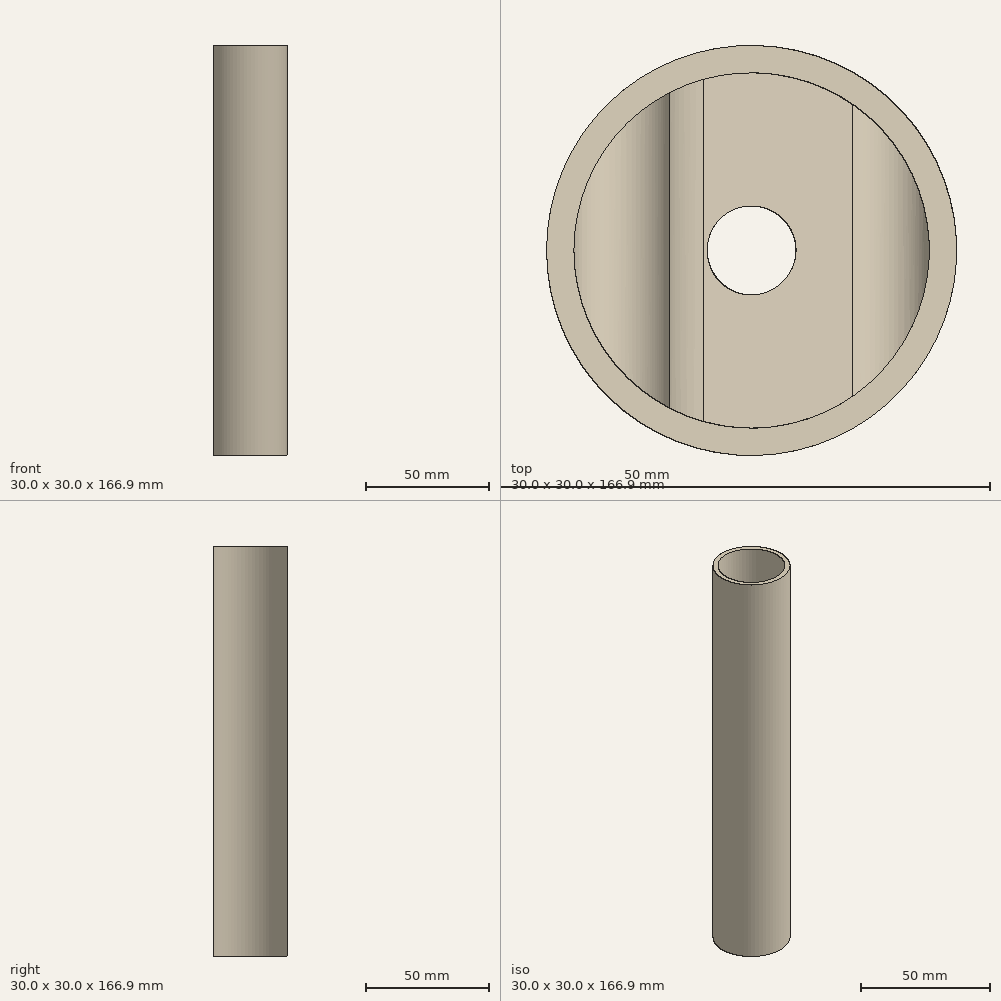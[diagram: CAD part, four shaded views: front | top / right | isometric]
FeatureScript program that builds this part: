
annotation { "Feature Type Name" : "Feature", "Feature Type Description" : "" }
export const myFeature = defineFeature(function(context is Context, id is Id, definition is map)
    precondition{}
    {
        {
            var Q0;
            Q0=qCreatedBy(makeId("Front.planeOp"),FACE);
            var sketch = newSketch(context, id + "F0", { "sketchPlane" : qUnion([Q0])});
            skLineSegment(sketch, "E0.bottom", {"start": v(15, 0) * mm, "end": v(0, 0) * mm, "construction": true});
            skLineSegment(sketch, "E0.top", {"start": v(15, 160) * mm, "end": v(0, 160) * mm, "construction": true});
            skLineSegment(sketch, "E0.left", {"start": v(15, 0) * mm, "end": v(15, 160) * mm, "construction": true});
            skLineSegment(sketch, "E0.right", {"start": v(0, 0) * mm, "end": v(0, 160) * mm, "construction": true});
            skLineSegment(sketch, "E1.MirrorCS", {"start": v(-15, 0) * mm, "end": v(-15, 160) * mm, "construction": true});
            skLineSegment(sketch, "E2", {"start": v(13, 0) * mm, "end": v(13, 160) * mm, "construction": true});
            skLineSegment(sketch, "E3.MirrorCS", {"start": v(-13, 0) * mm, "end": v(-13, 160) * mm, "construction": true});
            skLineSegment(sketch, "E4.MirrorCS", {"start": v(-15, 0) * mm, "end": v(0, 0) * mm, "construction": true});
            skLineSegment(sketch, "E5.MirrorCS", {"start": v(-15, 160) * mm, "end": v(0, 160) * mm, "construction": true});
            skLineSegment(sketch, "E6", {"start": v(3.5, 0) * mm, "end": v(3.5, 160) * mm, "construction": true});
            skLineSegment(sketch, "E7.MirrorCS", {"start": v(-3.5, 0) * mm, "end": v(-3.5, 160) * mm, "construction": true});
            skSolve(sketch);
        }
        {
            var Q0;
            Q0=qCreatedBy(makeId("Front.planeOp"),FACE);
            var sketch = newSketch(context, id + "F1", { "sketchPlane" : qUnion([Q0])});
            skArc(sketch, "E8", {"start": v(-13.08, 33) * mm, "mid": v(-9.35, 29.44) * mm, "end": v(-6, 33.35) * mm});
            skArc(sketch, "E9", {"start": v(-13.08, 23.7) * mm, "mid": v(-10.14, 27.9) * mm, "end": v(-5.15, 26.66) * mm});
            skArc(sketch, "E10", {"start": v(7.37, 17.07) * mm, "mid": v(10.97, 16.65) * mm, "end": v(12.98, 19.67) * mm});
            skArc(sketch, "E11", {"start": v(12.98, 9.26) * mm, "mid": v(11.86, 12.31) * mm, "end": v(8.97, 13.81) * mm});
            skArc(sketch, "E12", {"start": v(8.97, 13.81) * mm, "mid": v(7.8, 14.12) * mm, "end": v(6.74, 14.74) * mm});
            skArc(sketch, "E13", {"start": v(-6, 33.35) * mm, "mid": v(-5.17, 30.52) * mm, "end": v(-3.56, 28.05) * mm});
            skLineSegment(sketch, "E14", {"start": v(-13.08, 33) * mm, "end": v(-13.08, 23.7) * mm});
            skLineSegment(sketch, "E15", {"start": v(-3.56, 28.05) * mm, "end": v(7.37, 17.07) * mm});
            skLineSegment(sketch, "E16", {"start": v(-5.15, 26.66) * mm, "end": v(6.74, 14.74) * mm});
            skLineSegment(sketch, "E17", {"start": v(12.98, 9.26) * mm, "end": v(12.98, 19.67) * mm});
            skArc(sketch, "E18", {"start": v(-13.08, 54.39) * mm, "mid": v(-9.35, 50.84) * mm, "end": v(-6, 54.74) * mm});
            skArc(sketch, "E19", {"start": v(-13.08, 45.09) * mm, "mid": v(-10.14, 49.3) * mm, "end": v(-5.15, 48.06) * mm});
            skArc(sketch, "E20", {"start": v(7.37, 38.46) * mm, "mid": v(10.97, 38.05) * mm, "end": v(12.98, 41.07) * mm});
            skArc(sketch, "E21", {"start": v(12.98, 30.65) * mm, "mid": v(11.86, 33.7) * mm, "end": v(8.97, 35.2) * mm});
            skArc(sketch, "E22", {"start": v(8.97, 35.2) * mm, "mid": v(7.8, 35.52) * mm, "end": v(6.74, 36.14) * mm});
            skArc(sketch, "E23", {"start": v(-6, 54.74) * mm, "mid": v(-5.17, 51.91) * mm, "end": v(-3.56, 49.44) * mm});
            skLineSegment(sketch, "E24", {"start": v(-13.08, 54.39) * mm, "end": v(-13.08, 45.09) * mm});
            skLineSegment(sketch, "E25", {"start": v(-3.56, 49.44) * mm, "end": v(7.37, 38.46) * mm});
            skLineSegment(sketch, "E26", {"start": v(-5.15, 48.06) * mm, "end": v(6.74, 36.14) * mm});
            skLineSegment(sketch, "E27", {"start": v(12.98, 30.65) * mm, "end": v(12.98, 41.07) * mm});
            skArc(sketch, "E28", {"start": v(-13.08, 78.1) * mm, "mid": v(-9.35, 74.56) * mm, "end": v(-6, 78.46) * mm});
            skArc(sketch, "E29", {"start": v(-13.08, 68.8) * mm, "mid": v(-10.14, 73.02) * mm, "end": v(-5.15, 71.78) * mm});
            skArc(sketch, "E30", {"start": v(7.37, 62.18) * mm, "mid": v(10.97, 61.77) * mm, "end": v(12.98, 64.79) * mm});
            skArc(sketch, "E31", {"start": v(12.98, 54.37) * mm, "mid": v(11.86, 57.42) * mm, "end": v(8.97, 58.93) * mm});
            skArc(sketch, "E32", {"start": v(8.97, 58.93) * mm, "mid": v(7.8, 59.24) * mm, "end": v(6.74, 59.86) * mm});
            skArc(sketch, "E33", {"start": v(-6, 78.46) * mm, "mid": v(-5.17, 75.63) * mm, "end": v(-3.56, 73.16) * mm});
            skLineSegment(sketch, "E34", {"start": v(-13.08, 78.1) * mm, "end": v(-13.08, 68.8) * mm});
            skLineSegment(sketch, "E35", {"start": v(-3.56, 73.16) * mm, "end": v(7.37, 62.18) * mm});
            skLineSegment(sketch, "E36", {"start": v(-5.15, 71.78) * mm, "end": v(6.74, 59.86) * mm});
            skLineSegment(sketch, "E37", {"start": v(12.98, 54.37) * mm, "end": v(12.98, 64.79) * mm});
            skArc(sketch, "E38", {"start": v(-13.08, 104.36) * mm, "mid": v(-9.35, 100.8) * mm, "end": v(-6, 104.71) * mm});
            skArc(sketch, "E39", {"start": v(-13.08, 95.06) * mm, "mid": v(-10.14, 99.27) * mm, "end": v(-5.15, 98.03) * mm});
            skArc(sketch, "E40", {"start": v(7.37, 88.43) * mm, "mid": v(10.97, 88.02) * mm, "end": v(12.98, 91.04) * mm});
            skArc(sketch, "E41", {"start": v(12.98, 80.62) * mm, "mid": v(11.86, 83.68) * mm, "end": v(8.97, 85.18) * mm});
            skArc(sketch, "E42", {"start": v(8.97, 85.18) * mm, "mid": v(7.8, 85.49) * mm, "end": v(6.74, 86.1) * mm});
            skArc(sketch, "E43", {"start": v(-6, 104.71) * mm, "mid": v(-5.17, 101.88) * mm, "end": v(-3.56, 99.41) * mm});
            skLineSegment(sketch, "E44", {"start": v(-13.08, 104.36) * mm, "end": v(-13.08, 95.06) * mm});
            skLineSegment(sketch, "E45", {"start": v(-3.56, 99.41) * mm, "end": v(7.37, 88.43) * mm});
            skLineSegment(sketch, "E46", {"start": v(-5.15, 98.03) * mm, "end": v(6.74, 86.1) * mm});
            skLineSegment(sketch, "E47", {"start": v(12.98, 80.62) * mm, "end": v(12.98, 91.04) * mm});
            skArc(sketch, "E48", {"start": v(-13.08, 131.7) * mm, "mid": v(-9.35, 128.14) * mm, "end": v(-6, 132.05) * mm});
            skArc(sketch, "E49", {"start": v(-13.08, 122.4) * mm, "mid": v(-10.14, 126.6) * mm, "end": v(-5.15, 125.36) * mm});
            skArc(sketch, "E50", {"start": v(7.37, 115.77) * mm, "mid": v(10.97, 115.36) * mm, "end": v(12.98, 118.37) * mm});
            skArc(sketch, "E51", {"start": v(12.98, 107.96) * mm, "mid": v(11.86, 111.01) * mm, "end": v(8.97, 112.51) * mm});
            skArc(sketch, "E52", {"start": v(8.97, 112.51) * mm, "mid": v(7.8, 112.82) * mm, "end": v(6.74, 113.44) * mm});
            skArc(sketch, "E53", {"start": v(-6, 132.05) * mm, "mid": v(-5.17, 129.22) * mm, "end": v(-3.56, 126.75) * mm});
            skLineSegment(sketch, "E54", {"start": v(-13.08, 131.7) * mm, "end": v(-13.08, 122.4) * mm});
            skLineSegment(sketch, "E55", {"start": v(-3.56, 126.75) * mm, "end": v(7.37, 115.77) * mm});
            skLineSegment(sketch, "E56", {"start": v(-5.15, 125.36) * mm, "end": v(6.74, 113.44) * mm});
            skLineSegment(sketch, "E57", {"start": v(12.98, 107.96) * mm, "end": v(12.98, 118.37) * mm});
            skSolve(sketch);
        }
        {
            var Q0;
            Q0 = qSketchRegion(id + "F1", true);
            extrude(context, id + "F2", {"entities" : qUnion([Q0]), "depth" : 15 * mm, "hasSecondDirection" : true, "secondDirectionOppositeDirection" : true, "secondDirectionDepth" : 15 * mm});
        }
        {
            var Q0;
            Q0=qCreatedBy(makeId("Top.planeOp"),FACE);
            var sketch = newSketch(context, id + "F3", { "sketchPlane" : qUnion([Q0])});
            skCircle(sketch, "E58", {"center": v(0, 0) * mm, "radius": 13 * mm});
            skCircle(sketch, "E59", {"center": v(0, 0) * mm, "radius": 20.3 * mm});
            skSolve(sketch);
        }
        {
            var Q0;
            Q0=makeQuery(id+"F3.imprint","IMPRINT",FACE,{"disambiguationData":[TD([[makeQuery(id+"F3.imprint","IMPRINT",EDGE,{"derivedFrom":sQuery(id+"F3.wireOp",EDGE,"E58")}),-1.0]])]});
            extrude(context, id + "F4", {"entities" : qUnion([Q0]), "operationType" : NewBodyOperationType.REMOVE, "endBound" : BoundingType.THROUGH_ALL, "depth" : 25 * mm});
        }
        {
            var Q0;
            Q0=qCreatedBy(makeId("Front.planeOp"),FACE);
            var sketch = newSketch(context, id + "F5", { "sketchPlane" : qUnion([Q0])});
            skLineSegment(sketch, "E60", {"start": v(0, 3.1) * mm, "end": v(15, 3.1) * mm});
            skLineSegment(sketch, "E61", {"start": v(15, 3.1) * mm, "end": v(15, 154.93) * mm});
            skArc(sketch, "E62", {"start": v(13, 9.41) * mm, "mid": v(10.05, 5.75) * mm, "end": v(5.38, 6.28) * mm});
            skPoint(sketch, "E63", {"position": v(15, 154.93) * mm});
            skLineSegment(sketch, "E64", {"start": v(13, 127.81) * mm, "end": v(13, 9.41) * mm});
            skLineSegment(sketch, "E65", {"start": v(13, 169.99) * mm, "end": v(15, 169.99) * mm});
            skLineSegment(sketch, "E66", {"start": v(15, 169.99) * mm, "end": v(15, 154.93) * mm});
            skLineSegment(sketch, "E67", {"start": v(13, 169.99) * mm, "end": v(13, 127.81) * mm});
            skLineSegment(sketch, "E68", {"start": v(5.38, 6.28) * mm, "end": v(0, 6.28) * mm});
            skLineSegment(sketch, "E69", {"start": v(0, 6.28) * mm, "end": v(0, 3.1) * mm});
            skSolve(sketch);
        }
        {
            var Q0;
            Q0 = qSketchRegion(id + "F5", true);
            var Q1;
            Q1=sQuery(id+"F0.wireOp",EDGE,"E0.right");
            revolve(context, id + "F6", {"entities" : qUnion([Q0]), "axis" : qUnion([Q1]), "revolveType" : RevolveType.FULL});
        }
        {
            var Q0;
            Q0=qCreatedBy(makeId("Top.planeOp"),FACE);
            var sketch = newSketch(context, id + "F7", { "sketchPlane" : qUnion([Q0])});
            skCircle(sketch, "E70", {"center": v(0, 0) * mm, "radius": 3.25 * mm});
            skSolve(sketch);
        }
        {
            var Q0;
            Q0 = qSketchRegion(id + "F7", true);
            var Q1;
            Q1=sQuery(id+"F7.wireOp",EDGE,"E70");
            extrude(context, id + "F8", {"entities" : qUnion([Q0]), "operationType" : NewBodyOperationType.REMOVE, "surfaceEntities" : qUnion([Q1]), "endBound" : BoundingType.THROUGH_ALL, "depth" : 25 * mm, "hasSecondDirection" : true, "secondDirectionOppositeDirection" : true, "secondDirectionDepth" : 25 * mm});
        }
    });
